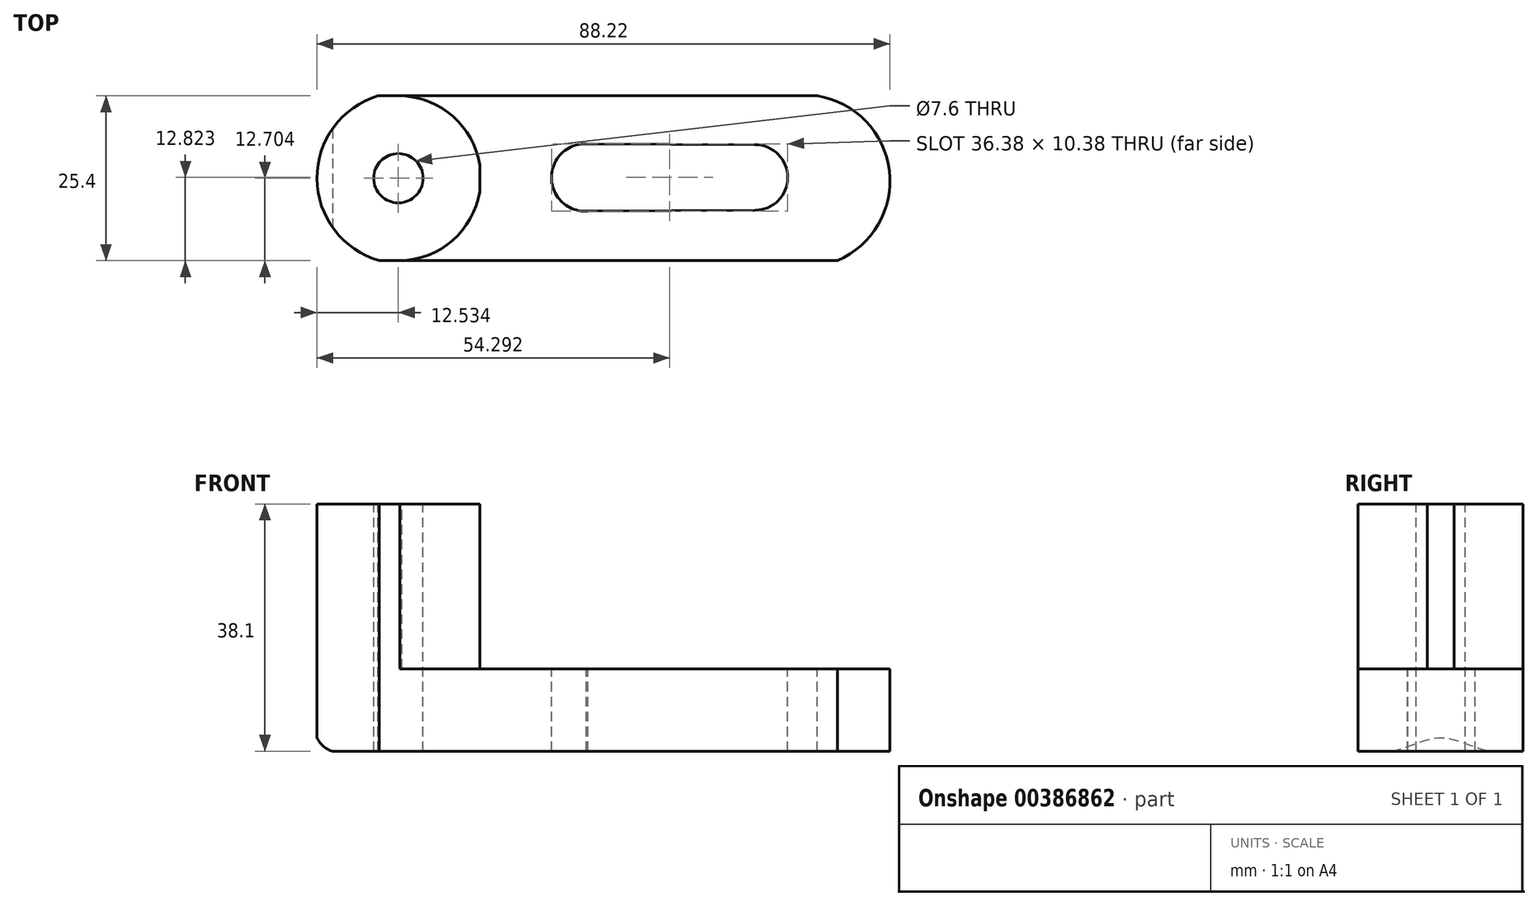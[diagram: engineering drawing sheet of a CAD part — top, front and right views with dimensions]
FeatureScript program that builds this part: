
annotation { "Feature Type Name" : "Feature", "Feature Type Description" : "" }
export const myFeature = defineFeature(function(context is Context, id is Id, definition is map)
    precondition{}
    {
        {
            var Q0;
            Q0=qCreatedBy(makeId("Front.planeOp"),FACE);
            var sketch = newSketch(context, id + "F0", { "sketchPlane" : qUnion([Q0])});
            skLineSegment(sketch, "E0", {"start": v(-25.4, 0) * mm, "end": v(-25.4, 38.1) * mm});
            skLineSegment(sketch, "E1", {"start": v(-25.4, 38.1) * mm, "end": v(0, 38.1) * mm});
            skLineSegment(sketch, "E2", {"start": v(0, 38.1) * mm, "end": v(0, 12.7) * mm});
            skLineSegment(sketch, "E3", {"start": v(0, 12.7) * mm, "end": v(63.5, 12.7) * mm});
            skLineSegment(sketch, "E4", {"start": v(63.5, 12.7) * mm, "end": v(63.5, 0) * mm});
            skLineSegment(sketch, "E5", {"start": v(63.5, 0) * mm, "end": v(-25.4, 0) * mm});
            skSolve(sketch);
        }
        {
            var Q0;
            Q0=makeQuery(id+"F0.imprint","IMPRINT",FACE,{"disambiguationData":[TD([[makeQuery(id+"F0.imprint","IMPRINT",EDGE,{"derivedFrom":sQuery(id+"F0.wireOp",EDGE,"E0")}),-1.0]])]});
            extrude(context, id + "F1", {"entities" : qUnion([Q0]), "depth" : 25.4 * mm});
        }
        {
            var Q0;
            Q0=makeQuery(id+"F1.opExtrude","CAP_FACE",FACE,{"disambiguationData":[OSD([sQuery(id+"F0.wireOp",EDGE,"E0"),sQuery(id+"F0.wireOp",EDGE,"E1"),sQuery(id+"F0.wireOp",EDGE,"E2"),sQuery(id+"F0.wireOp",EDGE,"E3"),sQuery(id+"F0.wireOp",EDGE,"E4"),sQuery(id+"F0.wireOp",EDGE,"E5")])],"isStart":false});
            var sketch = newSketch(context, id + "F2", { "sketchPlane" : qUnion([Q0])});
            skArc(sketch, "E6", {"start": v(-25.4, 3.94) * mm, "mid": v(-23.96, 0.67) * mm, "end": v(-20.46, 0) * mm});
            skSolve(sketch);
        }
        {
            var Q0;
            {var subQ0=sQuery(id+"F2.wireOp",EDGE,"E6");var subQ1=makeQuery(id+"F1.opExtrude","CAP_EDGE",EDGE,{"disambiguationData":[OSD([sQuery(id+"F0.wireOp",EDGE,"E0")])],"isStart":false});var subQ2=makeQuery(id+"F2.imprint","INTERSECT",VERTEX,{"disambiguationData":[OD(1.0)],"derivedFrom":[subQ1,subQ0]});Q0=makeQuery(id+"F2.imprint","IMPRINT",FACE,{"disambiguationData":[TD([[makeQuery(id+"F2.imprint","IMPRINT",EDGE,{"disambiguationData":[TD([[subQ2,-1.0]])],"derivedFrom":subQ0}),-1.0]])]});}
            extrude(context, id + "F3", {"entities" : qUnion([Q0]), "operationType" : NewBodyOperationType.REMOVE, "oppositeDirection" : true, "depth" : 25.4 * mm});
        }
        {
            var Q0;
            Q0=makeQuery(id+"F1.opExtrude","SWEPT_FACE",FACE,{"disambiguationData":[OSD([sQuery(id+"F0.wireOp",EDGE,"E3")])]});
            var sketch = newSketch(context, id + "F4", { "sketchPlane" : qUnion([Q0])});
            skArc(sketch, "E7", {"start": v(55.04, -25.4) * mm, "mid": v(63.05, -11.54) * mm, "end": v(51.96, 0) * mm});
            skSolve(sketch);
        }
        {
            var Q0;
            {var subQ0=sQuery(id+"F4.wireOp",EDGE,"E7");Q0=makeQuery(id+"F4.imprint","IMPRINT",FACE,{"disambiguationData":[TD([[makeQuery(id+"F4.imprint","IMPRINT",EDGE,{"derivedFrom":subQ0}),-1.0]])]});}
            extrude(context, id + "F5", {"entities" : qUnion([Q0]), "operationType" : NewBodyOperationType.REMOVE, "oppositeDirection" : true, "depth" : 25.4 * mm});
        }
        {
            var Q0;
            Q0=makeQuery(id+"F1.opExtrude","SWEPT_FACE",FACE,{"disambiguationData":[OSD([sQuery(id+"F0.wireOp",EDGE,"E1")])]});
            var sketch = newSketch(context, id + "F6", { "sketchPlane" : qUnion([Q0])});
            skArc(sketch, "E8", {"start": v(-15.66, 0) * mm, "mid": v(-25.07, -12.77) * mm, "end": v(-15.46, -25.4) * mm});
            skSolve(sketch);
        }
        {
            var Q0;
            {var subQ0=sQuery(id+"F6.wireOp",EDGE,"E8");Q0=makeQuery(id+"F6.imprint","IMPRINT",FACE,{"disambiguationData":[TD([[makeQuery(id+"F6.imprint","IMPRINT",EDGE,{"derivedFrom":subQ0}),-1.0]])]});}
            extrude(context, id + "F7", {"entities" : qUnion([Q0]), "operationType" : NewBodyOperationType.REMOVE, "oppositeDirection" : true, "depth" : 25.4 * mm});
        }
        {
            var Q0;
            Q0=makeQuery(id+"F7.boolean.opBoolean","COPY",FACE,{"derivedFrom":makeQuery(id+"F7.opExtrude","CAP_FACE",FACE,{"disambiguationData":[OSD([sQuery(id+"F0.wireOp",EDGE,"E0"),sQuery(id+"F0.wireOp",EDGE,"E1"),sQuery(id+"F6.wireOp",EDGE,"E8")])],"isStart":false})});
            var sketch = newSketch(context, id + "F8", { "sketchPlane" : qUnion([Q0])});
            skSolve(sketch);
        }
        {
            var Q0;
            {var subQ0=sQuery(id+"F6.wireOp",EDGE,"E8");Q0=makeQuery(id+"F8.imprint","IMPRINT",FACE,{"disambiguationData":[TD([[makeQuery(id+"F8.imprint","IMPRINT",EDGE,{"derivedFrom":makeQuery(id+"F7.boolean.opBoolean","COPY",EDGE,{"derivedFrom":makeQuery(id+"F7.opExtrude","CAP_EDGE",EDGE,{"disambiguationData":[OSD([subQ0])],"isStart":false})})}),-1.0]])]});}
            extrude(context, id + "F9", {"entities" : qUnion([Q0]), "operationType" : NewBodyOperationType.REMOVE, "oppositeDirection" : true, "depth" : 50.8 * mm});
        }
        {
            var Q0;
            Q0=qCreatedBy(makeId("Top.planeOp"),FACE);
            var sketch = newSketch(context, id + "F10", { "sketchPlane" : qUnion([Q0])});
            skArc(sketch, "E9", {"start": v(-6.24, -25.4) * mm, "mid": v(-0.32, -12.7) * mm, "end": v(-6.24, 0) * mm});
            skSolve(sketch);
        }
        {
            var Q0;
            Q0=sQuery(id+"F10.wireOp",EDGE,"E9");
            extrude(context, id + "F11", {"bodyType" : ToolBodyType.SURFACE, "surfaceEntities" : qUnion([Q0]), "depth" : 25.4 * mm});
        }
        {
            var Q0;
            Q0=makeQuery(id+"F1.opExtrude","SWEPT_FACE",FACE,{"disambiguationData":[OSD([sQuery(id+"F0.wireOp",EDGE,"E1")])]});
            var sketch = newSketch(context, id + "F12", { "sketchPlane" : qUnion([Q0])});
            skArc(sketch, "E10", {"start": v(-12.77, -25.4) * mm, "mid": v(0.16, -13.08) * mm, "end": v(-12, 0) * mm});
            skSolve(sketch);
        }
        {
            var Q0;
            {var subQ0=sQuery(id+"F12.wireOp",EDGE,"E10");var subQ1=sQuery(id+"F0.wireOp",EDGE,"E1");var subQ2=makeQuery(id+"F1.opExtrude","CAP_EDGE",EDGE,{"disambiguationData":[OSD([subQ1])],"isStart":true});var subQ3=makeQuery(id+"F12.imprint","INTERSECT",VERTEX,{"derivedFrom":[subQ2,subQ0]});Q0=makeQuery(id+"F12.imprint","IMPRINT",FACE,{"disambiguationData":[TD([[makeQuery(id+"F12.imprint","IMPRINT",EDGE,{"disambiguationData":[TD([[subQ3,1.0]])],"derivedFrom":subQ0}),-1.0]])]});}
            var Q1;
            {var subQ0=sQuery(id+"F12.wireOp",EDGE,"E10");var subQ1=sQuery(id+"F0.wireOp",EDGE,"E1");var subQ2=makeQuery(id+"F1.opExtrude","CAP_EDGE",EDGE,{"disambiguationData":[OSD([subQ1])],"isStart":false});var subQ3=makeQuery(id+"F12.imprint","INTERSECT",VERTEX,{"disambiguationData":[OD(1.0)],"derivedFrom":[subQ2,subQ0]});Q1=makeQuery(id+"F12.imprint","IMPRINT",FACE,{"disambiguationData":[TD([[makeQuery(id+"F12.imprint","IMPRINT",EDGE,{"disambiguationData":[TD([[subQ3,-1.0]])],"derivedFrom":subQ0}),-1.0]])]});}
            extrude(context, id + "F13", {"entities" : qUnion([Q0, Q1]), "operationType" : NewBodyOperationType.REMOVE, "oppositeDirection" : true, "depth" : 25.4 * mm});
        }
        {
            var Q0;
            Q0=makeQuery(id+"F1.opExtrude","SWEPT_FACE",FACE,{"disambiguationData":[OSD([sQuery(id+"F0.wireOp",EDGE,"E1")])]});
            var sketch = newSketch(context, id + "F14", { "sketchPlane" : qUnion([Q0])});
            skCircle(sketch, "E11", {"center": v(-12.54, -12.7) * mm, "radius": 3.8 * mm});
            skSolve(sketch);
        }
        {
            var Q0;
            Q0=makeQuery(id+"F14.imprint","IMPRINT",FACE,{"disambiguationData":[TD([[makeQuery(id+"F14.imprint","IMPRINT",EDGE,{"derivedFrom":sQuery(id+"F14.wireOp",EDGE,"E11")}),1.0]])]});
            extrude(context, id + "F15", {"entities" : qUnion([Q0]), "operationType" : NewBodyOperationType.REMOVE, "oppositeDirection" : true, "depth" : 76.2 * mm});
        }
        {
            var Q0;
            {var subQ0=sQuery(id+"F0.wireOp",EDGE,"E1");var subQ1=makeQuery(id+"F1.opExtrude","CAP_EDGE",EDGE,{"disambiguationData":[OSD([subQ0])],"isStart":true});var subQ2=sQuery(id+"F0.wireOp",EDGE,"E2");var subQ3=makeQuery(id+"F1.opExtrude","SWEPT_EDGE",EDGE,{"disambiguationData":[OSD([subQ0,subQ2])]});var subQ4=makeQuery(id+"F12.imprint","INTERSECT",VERTEX,{"derivedFrom":[subQ3,subQ1]});var subQ5=sQuery(id+"F12.wireOp",EDGE,"E10");var subQ6=makeQuery(id+"F12.imprint","INTERSECT",VERTEX,{"derivedFrom":[subQ1,subQ5]});var subQ8=makeQuery(id+"F1.opExtrude","CAP_EDGE",EDGE,{"disambiguationData":[OSD([subQ0])],"isStart":false});var subQ9=makeQuery(id+"F12.imprint","INTERSECT",VERTEX,{"derivedFrom":[subQ3,subQ8]});var subQ10=makeQuery(id+"F12.imprint","INTERSECT",VERTEX,{"disambiguationData":[OD(1.0)],"derivedFrom":[subQ8,subQ5]});Q0=makeQuery(id+"F13.boolean.opBoolean","MERGE",FACE,{"derivedFrom":[makeQuery(id+"F1.opExtrude","SWEPT_FACE",FACE,{"disambiguationData":[OSD([sQuery(id+"F0.wireOp",EDGE,"E3")])]}),makeQuery(id+"F13.opExtrude","CAP_FACE",FACE,{"disambiguationData":[OSD([subQ0,subQ2,subQ5]),TDD([makeQuery(id+"F12.imprint","IMPRINT",EDGE,{"disambiguationData":[TD([[subQ10,-1.0]])],"derivedFrom":subQ5}),makeQuery(id+"F12.imprint","IMPRINT",EDGE,{"disambiguationData":[TD([[subQ9,-1.0]])],"derivedFrom":subQ3}),makeQuery(id+"F12.imprint","IMPRINT",EDGE,{"disambiguationData":[TD([[subQ10,-1.0]])],"derivedFrom":subQ8})])],"isStart":false}),makeQuery(id+"F13.opExtrude","CAP_FACE",FACE,{"disambiguationData":[OSD([subQ0,subQ2,subQ5]),TDD([makeQuery(id+"F12.imprint","IMPRINT",EDGE,{"disambiguationData":[TD([[subQ6,1.0]])],"derivedFrom":subQ5}),makeQuery(id+"F12.imprint","IMPRINT",EDGE,{"disambiguationData":[TD([[subQ4,1.0]])],"derivedFrom":subQ3}),makeQuery(id+"F12.imprint","IMPRINT",EDGE,{"disambiguationData":[TD([[subQ6,-1.0]])],"derivedFrom":subQ1})])],"isStart":false})]});}
            var sketch = newSketch(context, id + "F16", { "sketchPlane" : qUnion([Q0])});
            skCircle(sketch, "E12", {"center": v(16.23, -12.58) * mm, "radius": 5.2 * mm});
            skCircle(sketch, "E13", {"center": v(42.36, -12.58) * mm, "radius": 5.05 * mm});
            skLineSegment(sketch, "E14", {"start": v(16.42, -7.38) * mm, "end": v(42.39, -7.53) * mm});
            skLineSegment(sketch, "E15", {"start": v(16.62, -17.77) * mm, "end": v(42.38, -17.64) * mm});
            skSolve(sketch);
        }
        {
            var Q0;
            {var subQ0=sQuery(id+"F16.wireOp",EDGE,"E12");var subQ1=makeQuery(id+"F16.imprint","INTERSECT",VERTEX,{"derivedFrom":[subQ0,sQuery(id+"F16.wireOp",EDGE,"E14")]});Q0=makeQuery(id+"F16.imprint","IMPRINT",FACE,{"disambiguationData":[TD([[makeQuery(id+"F16.imprint","IMPRINT",EDGE,{"disambiguationData":[TD([[subQ1,-1.0]])],"derivedFrom":subQ0}),1.0]])]});}
            var Q1;
            {var subQ0=sQuery(id+"F16.wireOp",EDGE,"E13");var subQ1=makeQuery(id+"F16.imprint","INTERSECT",VERTEX,{"derivedFrom":[subQ0,sQuery(id+"F16.wireOp",EDGE,"E14")]});Q1=makeQuery(id+"F16.imprint","IMPRINT",FACE,{"disambiguationData":[TD([[makeQuery(id+"F16.imprint","IMPRINT",EDGE,{"disambiguationData":[TD([[subQ1,-1.0]])],"derivedFrom":subQ0}),1.0]])]});}
            var Q2;
            {var subQ0=sQuery(id+"F16.wireOp",EDGE,"E14");Q2=makeQuery(id+"F16.imprint","IMPRINT",FACE,{"disambiguationData":[TD([[makeQuery(id+"F16.imprint","IMPRINT",EDGE,{"derivedFrom":subQ0}),-1.0]])]});}
            extrude(context, id + "F17", {"entities" : qUnion([Q0, Q1, Q2]), "operationType" : NewBodyOperationType.REMOVE, "oppositeDirection" : true, "depth" : 25.4 * mm});
        }
    });
